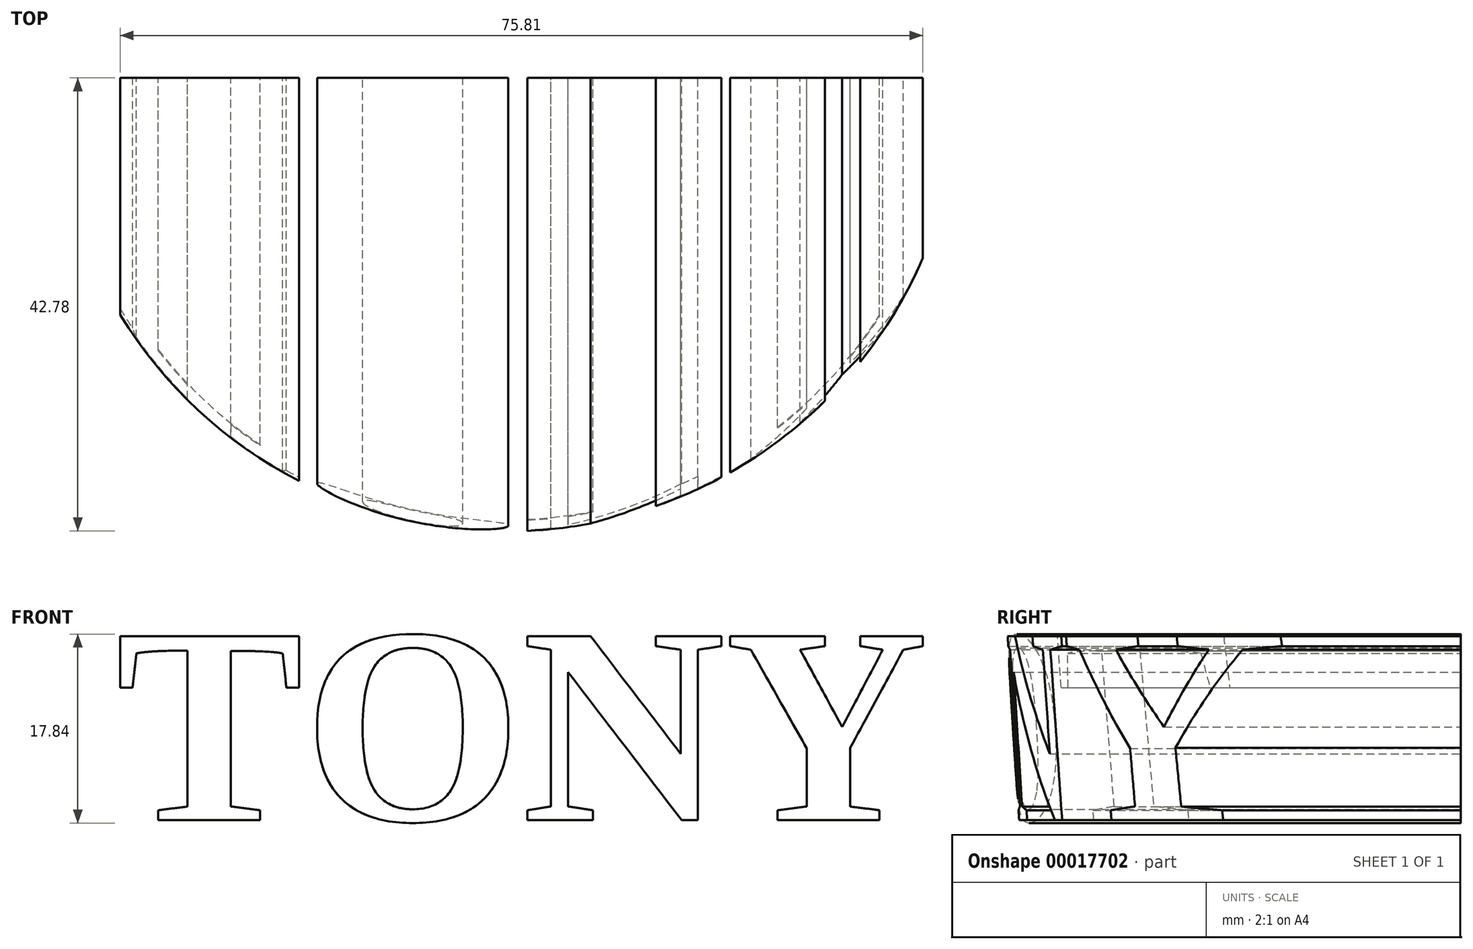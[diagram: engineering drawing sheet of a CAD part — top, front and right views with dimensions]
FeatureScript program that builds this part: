
annotation { "Feature Type Name" : "Feature", "Feature Type Description" : "" }
export const myFeature = defineFeature(function(context is Context, id is Id, definition is map)
    precondition{}
    {
        {
            var Q0;
            Q0=qCreatedBy(makeId("Top.planeOp"),FACE);
            var sketch = newSketch(context, id + "F0", { "sketchPlane" : qUnion([Q0])});
            skCircle(sketch, "E0", {"center": v(0, 0) * mm, "radius": 38.1 * mm});
            skSolve(sketch);
        }
        {
            var Q0;
            Q0=qCreatedBy(makeId("Top.planeOp"),FACE);
            cPlane(context, id + "F1", {"entities" : qUnion([Q0]), "cplaneType" : CPlaneType.OFFSET, "offset" : 101.6 * mm, "width" : 152.4 * mm, "height" : 152.4 * mm});
        }
        {
            var Q0;
            Q0=qCreatedBy(id+"F1.planeOp",FACE);
            var sketch = newSketch(context, id + "F2", { "sketchPlane" : qUnion([Q0])});
            skPoint(sketch, "E1.0", {"position": v(0, 0) * mm});
            skCircle(sketch, "E2", {"center": v(0, 0) * mm, "radius": 44.45 * mm});
            skSolve(sketch);
        }
        {
            var Q0;
            Q0=makeQuery(id+"F2.imprint","IMPRINT",FACE,{"disambiguationData":[TD([[makeQuery(id+"F2.imprint","IMPRINT",EDGE,{"derivedFrom":sQuery(id+"F2.wireOp",EDGE,"E2")}),1.0]])]});
            var Q1;
            Q1=makeQuery(id+"F0.imprint","IMPRINT",FACE,{"disambiguationData":[TD([[makeQuery(id+"F0.imprint","IMPRINT",EDGE,{"derivedFrom":sQuery(id+"F0.wireOp",EDGE,"E0")}),1.0]])]});
            loft(context, id + "F3", {"sheetProfilesArray" : [{ "sheetProfileEntities" : qUnion([Q0]) }, { "sheetProfileEntities" : qUnion([Q1]) }]});
        }
        {
            var Q0;
            Q0=qCreatedBy(makeId("Front.planeOp"),FACE);
            var sketch = newSketch(context, id + "F4", { "sketchPlane" : qUnion([Q0])});
            skText(sketch, "E3", { "text": "TONY", "fontName": "Tinos-Bold.ttf"});
            const initialGuessF4  = {"E3": [-0.03692, 0.05816, 1, 0, 0.01912]};
            skSetInitialGuess(sketch, initialGuessF4);
            skSolve(sketch);
        }
        {
            var Q0;
            Q0 = qSketchRegion(id + "F4", true);
            extrude(context, id + "F5", {"entities" : qUnion([Q0]), "operationType" : NewBodyOperationType.INTERSECT, "depth" : 47.04 * mm});
        }
    });
